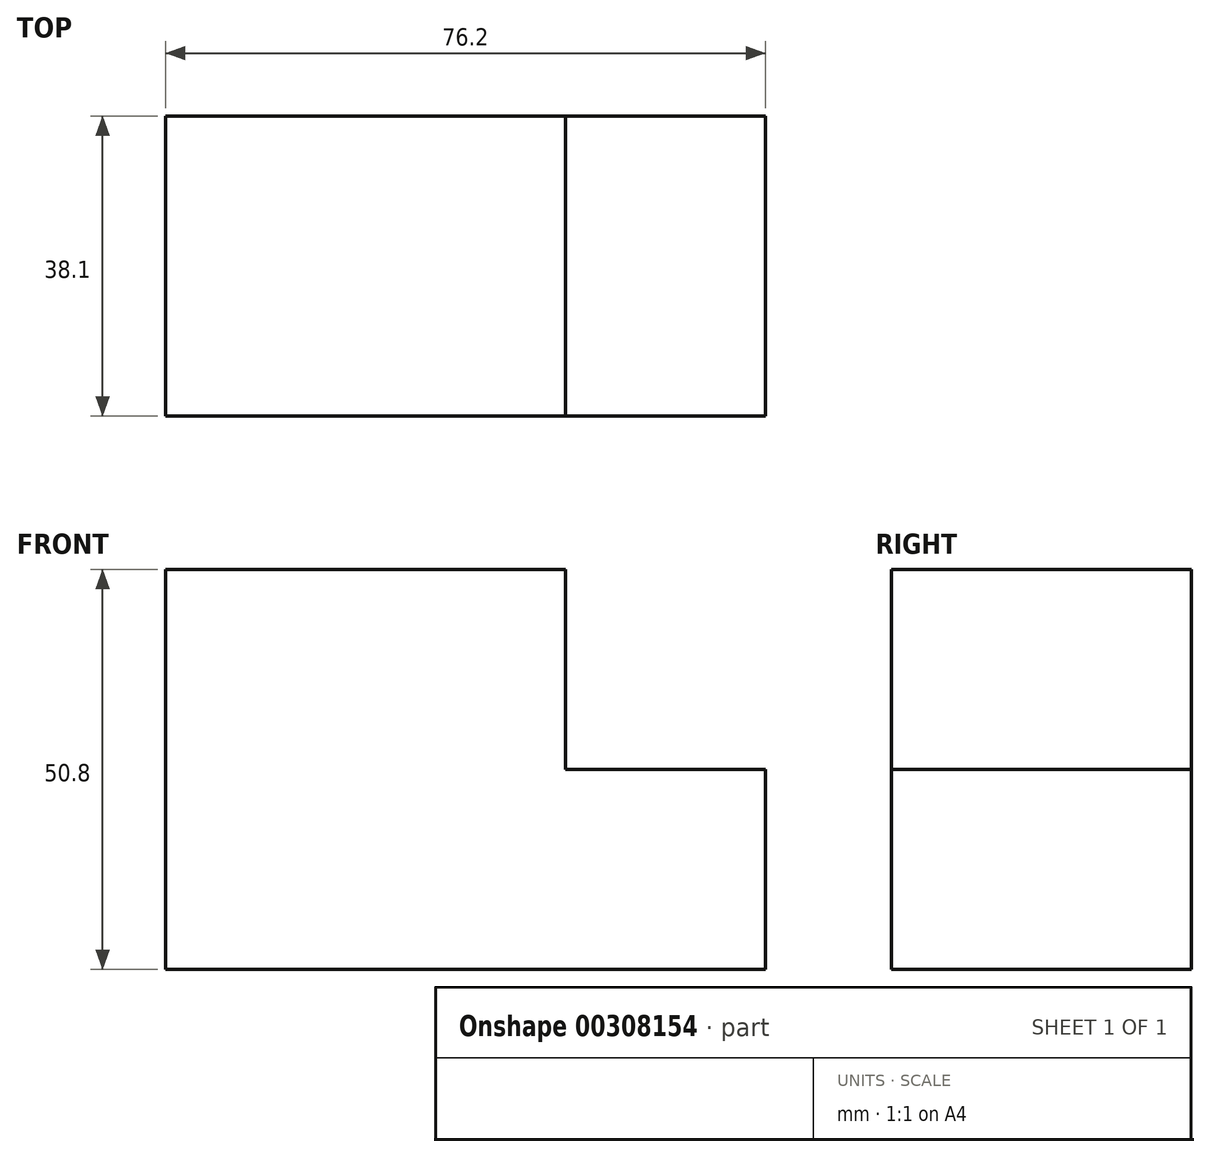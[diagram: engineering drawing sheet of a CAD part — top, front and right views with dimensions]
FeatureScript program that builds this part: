
annotation { "Feature Type Name" : "Feature", "Feature Type Description" : "" }
export const myFeature = defineFeature(function(context is Context, id is Id, definition is map)
    precondition{}
    {
        {
            var Q0;
            Q0=qCreatedBy(makeId("Front.planeOp"),FACE);
            var sketch = newSketch(context, id + "F0", { "sketchPlane" : qUnion([Q0])});
            skLineSegment(sketch, "E0", {"start": v(-47.23, -36.37) * mm, "end": v(28.97, -36.37) * mm});
            skLineSegment(sketch, "E1", {"start": v(-47.23, -36.37) * mm, "end": v(-47.23, 14.43) * mm});
            skLineSegment(sketch, "E2", {"start": v(-47.23, 14.43) * mm, "end": v(3.57, 14.43) * mm});
            skLineSegment(sketch, "E3", {"start": v(3.57, 14.43) * mm, "end": v(3.57, -10.97) * mm});
            skLineSegment(sketch, "E4", {"start": v(3.57, -10.97) * mm, "end": v(28.97, -10.97) * mm});
            skLineSegment(sketch, "E5", {"start": v(28.97, -10.97) * mm, "end": v(28.97, -36.37) * mm});
            skSolve(sketch);
        }
        {
            var Q0;
            Q0=makeQuery(id+"F0.imprint","IMPRINT",FACE,{"disambiguationData":[TD([[makeQuery(id+"F0.imprint","IMPRINT",EDGE,{"derivedFrom":sQuery(id+"F0.wireOp",EDGE,"E0")}),1.0]])]});
            extrude(context, id + "F1", {"entities" : qUnion([Q0]), "oppositeDirection" : true, "depth" : 38.1 * mm});
        }
    });
